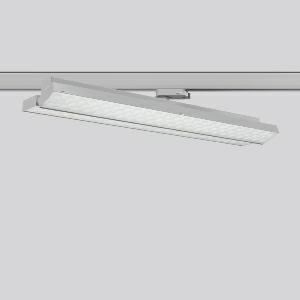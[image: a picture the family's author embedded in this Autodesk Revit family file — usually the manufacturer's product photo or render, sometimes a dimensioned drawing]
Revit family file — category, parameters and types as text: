
# Revit family: tx-move_742161_004_76_9d42
name_source: partatom
category: Lighting Fixtures
units: mm (PartAtom-declared; Revit-internal decimal feet)

## family parameters
Cut with Voids When Loaded = No
Host = Face
Light Source = No
Part Type = Normal
Room Calculation Point = No
Round Connector Dimension = Use Diameter
Shared = No

## types (1)
- MultiLumen 1 (1 x LED Modul 830, 2900 lm, 3000)
    Apparent Load = 41 VA
    CIE Flux Codes = 90 97 99 100 100
    Color Rendering = 80
    Color Temperature = 3000
    Default Elevation = 1800 mm
    Description = Series: TX-MOVE
Multifunctional surface-mounted spotlight for area lighting. Very flat design. Housing: sheet steel, powder-coated. Rotation range: 356°. Swivel range: 90°. Consistent alignment possible with visible tilt scale. High-efficiency LED units with optimum light control thanks to clear plastic (PC) lens optics. Spezielle Mikrostrukturen reduzieren Gelbsaum. Symmetrical light distribution. With adapter for RZB 3-circuit DALI tracks. Suitable for Track on ceiling. MultiLumen: Luminous flux adjustable in 3 steps. Factory setting is the highest luminous flux. Environmentally friendly and resource-saving due to replaceable and recyclable components. Very good glare control, ideal for till areas. 
Colour: silver, matt (approx. RAL 9006)
Length: 570 mm
Width: 119 mm
Height: 88 mm
Lamp: LED
Socket: without socket
Colour temperature: 3000K
Colour rendering index (CRI): 80
System power: 41 W
Rated luminous flux: 5800 lm
Luminous efficiency: 141 lm/W
System power 2: 57 W
Rated luminous flux 2: 7850 lm
Luminous efficiency 2: 138 lm/W
System power 3: 73 W
Rated luminous flux 3: 9600 lm
Luminous efficiency 3: 132 lm/W
Control gear: Dimmable EVG, DALI
Protection class: I
Type of protection: IP 20
    Height = 75 mm
    Lamp = 1 x LED Modul 830
    Lamp Light Flux = 2900 lm
    Lamp count = 1
    Length = 569 mm
    Lifetime = 50000 h
    Luminous efficacy = 141 lm/W
    Manufacturer = RZB
    ModVariant = No
    Model = 742161.004.76
    Mounting Place = Ceiling
    Mounting Type = Surface mounted
    Number of Poles = 1
    OnlyDefault = Yes
    Power Factor = 1
    Product Name = TX-MOVE
    Product group = Track mounted projectors
    ProductGroupID = 301
    Protection Class = Protection class I
    Protection Degree = IP 20
    RLX_Detail_Level = 1
    RLX_Emergency_Light_Flux = 0 lm
    RLX_Emergency_Type = 0
    RLX_Emergency_Type_DB = No
    RlxData = <blob elided: 33225 chars, md5=19a96242>
    Socket = socket
    Standby Power = 0 W
    System Light Flux = 5800 lm
    System Power = 41 W
    Type Comments = MultiLumen 1
    Type Image = 742162.004.jpg
    URL = http://relux.com
    VarID = multilumen_1
    Voltage = 0 V
    Weight = 0.00 kg
    Width = 119 mm

## geometry (parser evidence)
native form markers: Blend x4, Sweep x15
no freeform markers — native parametric forms only
